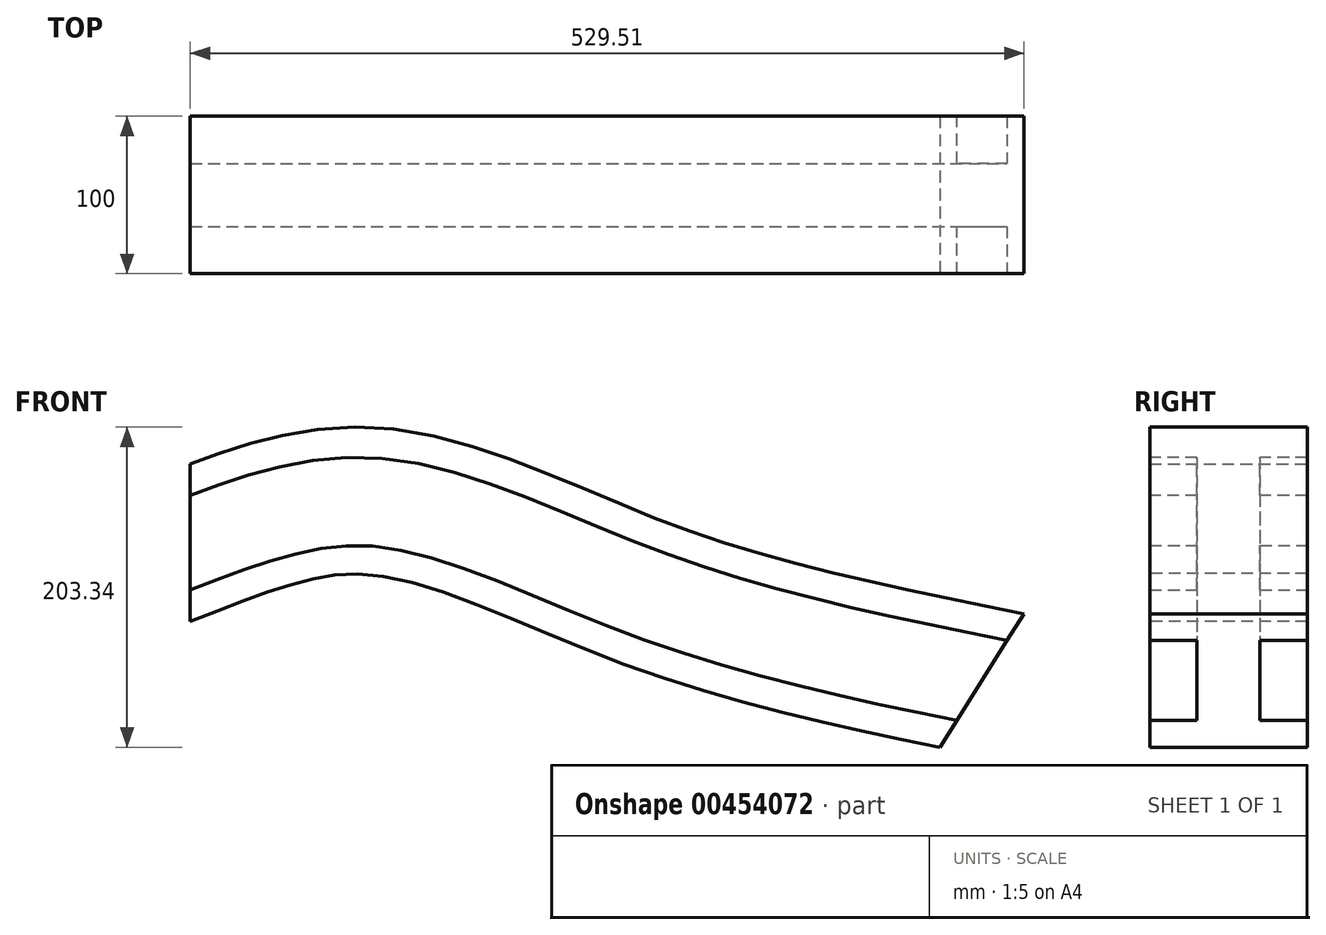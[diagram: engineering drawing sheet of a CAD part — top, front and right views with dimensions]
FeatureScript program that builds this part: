
annotation { "Feature Type Name" : "Feature", "Feature Type Description" : "" }
export const myFeature = defineFeature(function(context is Context, id is Id, definition is map)
    precondition{}
    {
        {
            var Q0;
            Q0=qCreatedBy(makeId("Right.planeOp"),FACE);
            var sketch = newSketch(context, id + "F0", { "sketchPlane" : qUnion([Q0])});
            skLineSegment(sketch, "E0", {"start": v(-50, 50) * mm, "end": v(50, 50) * mm});
            skLineSegment(sketch, "E1", {"start": v(50, 50) * mm, "end": v(50, 30) * mm});
            skLineSegment(sketch, "E2", {"start": v(50, 30) * mm, "end": v(20, 30) * mm});
            skLineSegment(sketch, "E3", {"start": v(20, 30) * mm, "end": v(20, -30) * mm});
            skLineSegment(sketch, "E4", {"start": v(20, -30) * mm, "end": v(50, -30) * mm});
            skLineSegment(sketch, "E5", {"start": v(50, -30) * mm, "end": v(50, -50) * mm});
            skLineSegment(sketch, "E6", {"start": v(50, -50) * mm, "end": v(-50, -50) * mm});
            skLineSegment(sketch, "E7", {"start": v(-50, -50) * mm, "end": v(-50, -30) * mm});
            skLineSegment(sketch, "E8", {"start": v(-50, -30) * mm, "end": v(-20, -30) * mm});
            skLineSegment(sketch, "E9", {"start": v(-20, -30) * mm, "end": v(-20, 30) * mm});
            skLineSegment(sketch, "E10", {"start": v(-20, 30) * mm, "end": v(-50, 30) * mm});
            skLineSegment(sketch, "E11", {"start": v(-50, 30) * mm, "end": v(-50, 50) * mm});
            skSolve(sketch);
        }
        {
            var Q0;
            Q0=qCreatedBy(makeId("Front.planeOp"),FACE);
            var sketch = newSketch(context, id + "F1", { "sketchPlane" : qUnion([Q0])});
            skFitSpline(sketch, "E12", {"points": [v(0, 0) * mm, v(119.98, 25.18) * mm, v(292.9, -33.56) * mm, v(502.93, -87.7) * mm], "startDerivative": vector(410.75, 153.65) * mm, "endDerivative": vector(570.84, -117.17) * mm});
            skSolve(sketch);
        }
        {
            var Q0;
            Q0=makeQuery(id+"F0.imprint","IMPRINT",FACE,{"disambiguationData":[TD([[makeQuery(id+"F0.imprint","IMPRINT",EDGE,{"derivedFrom":sQuery(id+"F0.wireOp",EDGE,"E0")}),-1.0]])]});
            var Q1;
            Q1=sQuery(id+"F1.wireOp",EDGE,"E12");
            sweep(context, id + "F2", {"profiles" : qUnion([Q0]), "path" : qUnion([Q1])});
        }
    });
